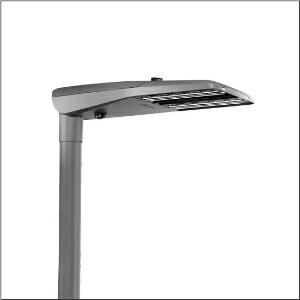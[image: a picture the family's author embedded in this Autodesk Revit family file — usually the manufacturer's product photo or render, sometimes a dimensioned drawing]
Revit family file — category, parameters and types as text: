
# Revit family: streetlight_sl_11_iq_midi___st1_0p1_0_5xc3k51y08me_73ea
name_source: partatom
category: Lighting Fixtures
units: mm (PartAtom-declared; Revit-internal decimal feet)

## family parameters
Cut with Voids When Loaded = No
Host = Face
Light Source = No
Part Type = Normal
Room Calculation Point = No
Round Connector Dimension = Use Diameter
Shared = No

## types (1)
- --- (1 x LED, 17540 lm, 122.7 W, 3000K)
    Apparent Load = 123 VA
    CIE Flux Codes = 32 65 95 100 100
    Color Rendering = 70
    Color Temperature = 3000K
    Default Elevation = 1800 mm
    Description = Streetlight SL 11 iQ midi, mast luminaire, primary light control with 3 zone facetted reflector, of plastic, silver coated, highly specular, primary optical cover: cover, of PMMA, transparent, light distribution: ST1.0P1.0, light emission: direct distribution, primary light characteristic: asymmetric, installation type: post-top, side-entry, LED, High Power LED, rated luminous flux: 17.540lm, luminous efficacy: 143lm/W, light colour: 730, colour temperature: 3000K, control: pre-setting: logarithmic dimming characteristic, Street-Remote, Auto-Match, Temp-Guard, Lumen-Switch, Night-Set, Smart-Wire, Light-Fading, Desk-Remote (wireless, voltage-free reading and setting of iQ features in the workshop via application-optimized NFC function/RFID function), optimised constant luminous flux control (CLO 2.0), with cable H07RN-F 5x 1.5mm², mains connection: 230..240V, AC, 50/60Hz, connection cable pre-assembled, cable length: 12,5m, start of lifetime: 123W, end of service life: 130W, reduction: 56W, luminaire housing, of diecast aluminium, powder-coated, Siteco® metallic grey (DB 702S), please order mast flange separately, inclination adjustable without tools: 0°, 5°, 10°, 15° (post-top) | 0°, -5°, -10°, -15° (side-entry), sealing non-destructively replaceable, multi-level sealing system, length: 780mm, width: 376mm, height: 118mm, mast flange for spigot size: 42mm (side-entry): 5XC10008XM4, 60/48mm (side-entry/post-top): 5XC10108XM2, 76/60mm (side-entry/post-top): 5XC10108XM1, equipment: Power, Smart Interface below and above, protection rating (complete): IP66, insulation class (complete): insulation class II (safety insulation), certification: CE, ENEC, VDE, UKCA, impact resistance: IK09, permissible operating ambient temperature for outdoor applications: -25..+50°C, standard-compliant lighting for roads and squares, Environmental Product Declaration (EPD) tested and certified by an independent institute, packaging unit: 1 piece

Light Distribution: ST1.0P1.0
    Height = 118 mm
    Lamp = 1 x LED
    Lamp Light Flux = 17540 lm
    Lamp Power = 122.7 W
    Lamp count = 1
    Length = 780 mm
    Luminous efficacy = 143 lm/W
    Manufacturer = Siteco
    ModVariant = No
    Model = 5XC3K51Y08ME
    Number of Poles = 1
    OnlyDefault = Yes
    Power Factor = 1
    Product Name = Streetlight SL 11 iQ midi | ST1.0P1.0
    Product group = mast luminaire | pylon top
    ProductGroupID = 6100
    Protection Class = Protection class II
    Protection Degree = IP 66
    RLX_Detail_Level = 1
    RLX_Emergency_Light_Flux = 0 lm
    RLX_Emergency_Type = 0
    RLX_Emergency_Type_DB = No
    RlxData = <blob elided: 69753 chars, md5=805ac466>
    Socket = socket
    Standby Power = 0 W
    System Light Flux = 17540 lm
    System Power = 123 W
    Type Comments = factory setting: luminous flux: 100 % | dim-lin: 254 | 553 mA
    Type Image = l_1004429.jpg
    URL = http://relux.com
    VarID = @adj_009109
    Voltage = 0 V
    Weight = 0.00 kg
    Width = 376 mm

## geometry (parser evidence)
native form markers: Blend x4, Sweep x10
no freeform markers — native parametric forms only
